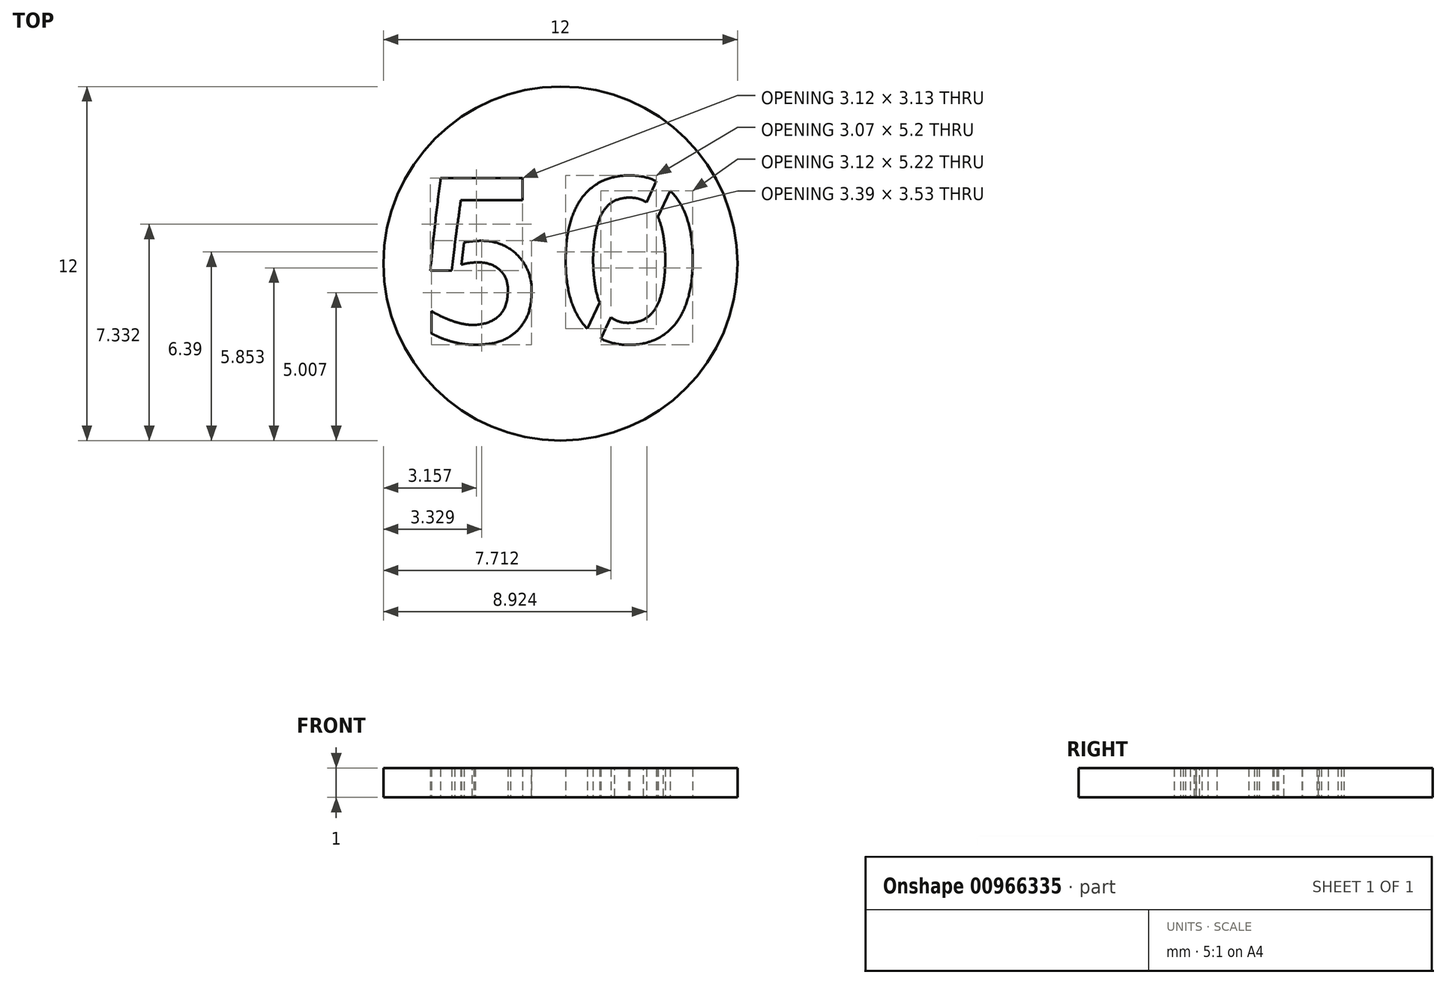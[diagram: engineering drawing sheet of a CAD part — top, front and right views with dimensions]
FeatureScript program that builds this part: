
annotation { "Feature Type Name" : "Feature", "Feature Type Description" : "" }
export const myFeature = defineFeature(function(context is Context, id is Id, definition is map)
    precondition{}
    {
        {
            var Q0;
            Q0=qCreatedBy(makeId("Top.planeOp"),FACE);
            var sketch = newSketch(context, id + "F0", { "sketchPlane" : qUnion([Q0])});
            skCircle(sketch, "E0", {"center": v(0, 0) * mm, "radius": 6 * mm});
            skSolve(sketch);
        }
        {
            var Q0;
            Q0=makeQuery(id+"F0.imprint","IMPRINT",FACE,{"disambiguationData":[TD([[makeQuery(id+"F0.imprint","IMPRINT",EDGE,{"derivedFrom":sQuery(id+"F0.wireOp",EDGE,"E0")}),1.0]])]});
            var sketch = newSketch(context, id + "F1", { "sketchPlane" : qUnion([Q0])});
            skText(sketch, "E1", { "text": "50\n", "fontName": "AllertaStencil-Regular.ttf"});
            const initialGuessF1  = {"E1": [-0.005, -0.00272, 1, 0, 0.00562]};
            skSetInitialGuess(sketch, initialGuessF1);
            skSolve(sketch);
        }
        {
            var Q0;
            Q0=makeQuery(id+"F0.imprint","IMPRINT",FACE,{"disambiguationData":[TD([[makeQuery(id+"F0.imprint","IMPRINT",EDGE,{"derivedFrom":sQuery(id+"F0.wireOp",EDGE,"E0")}),1.0]])]});
            extrude(context, id + "F2", {"entities" : qUnion([Q0]), "depth" : 1 * mm, "offsetDistance" : 25.4 * mm});
        }
        {
            var Q0;
            Q0=qSketchRegion(id+"F1",true);
            extrude(context, id + "F3", {"entities" : qUnion([Q0]), "operationType" : NewBodyOperationType.REMOVE, "depth" : 1.4 * mm, "offsetDistance" : 25.4 * mm});
        }
    });
